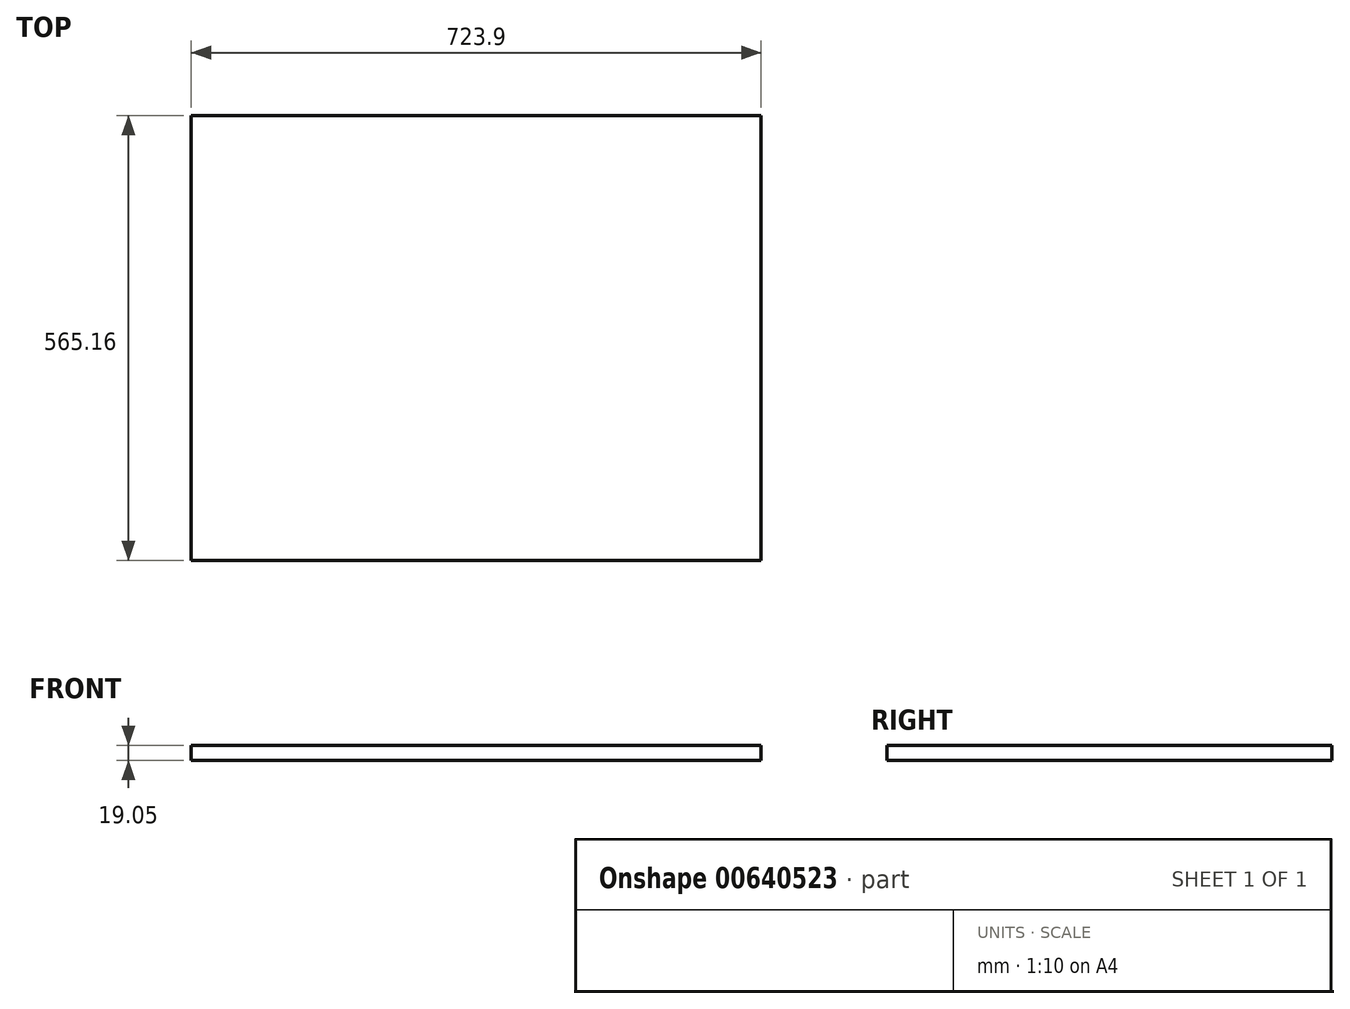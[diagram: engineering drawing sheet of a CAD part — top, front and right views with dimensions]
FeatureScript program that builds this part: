
annotation { "Feature Type Name" : "Feature", "Feature Type Description" : "" }
export const myFeature = defineFeature(function(context is Context, id is Id, definition is map)
    precondition{}
    {
        {
            var Q0;
            Q0=qCreatedBy(makeId("Top.planeOp"),FACE);
            var sketch = newSketch(context, id + "F0", { "sketchPlane" : qUnion([Q0])});
            skLineSegment(sketch, "E0.bottom", {"start": v(361.95, 282.58) * mm, "end": v(-361.95, 282.58) * mm});
            skLineSegment(sketch, "E0.top", {"start": v(361.95, -282.58) * mm, "end": v(-361.95, -282.58) * mm});
            skLineSegment(sketch, "E0.left", {"start": v(361.95, 282.57) * mm, "end": v(361.95, -282.58) * mm});
            skLineSegment(sketch, "E0.right", {"start": v(-361.95, 282.58) * mm, "end": v(-361.95, -282.58) * mm});
            skPoint(sketch, "E0.middle", {"position": v(0, 0) * mm});
            skSolve(sketch);
        }
        {
            var Q0;
            Q0=makeQuery(id+"F0.imprint","IMPRINT",FACE,{"disambiguationData":[TD([[makeQuery(id+"F0.imprint","IMPRINT",EDGE,{"derivedFrom":sQuery(id+"F0.wireOp",EDGE,"E0.bottom")}),1.0]])]});
            extrude(context, id + "F1", {"entities" : qUnion([Q0]), "depth" : 19.05 * mm, "offsetDistance" : 25.4 * mm});
        }
    });
